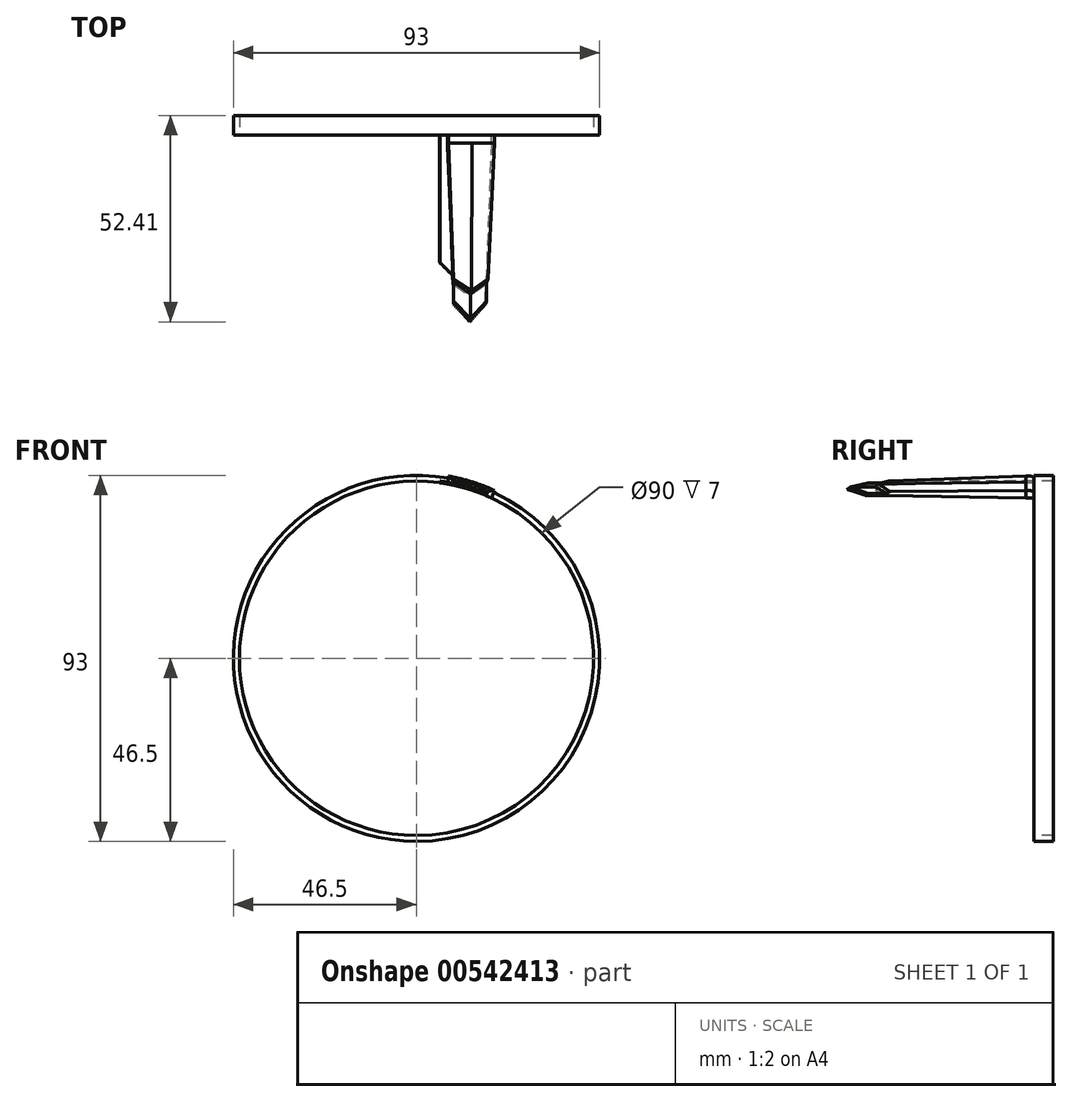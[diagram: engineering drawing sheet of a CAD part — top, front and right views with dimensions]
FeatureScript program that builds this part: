
annotation { "Feature Type Name" : "Feature", "Feature Type Description" : "" }
export const myFeature = defineFeature(function(context is Context, id is Id, definition is map)
    precondition{}
    {
        {
            var Q0;
            Q0=qCreatedBy(makeId("Front.planeOp"),FACE);
            var sketch = newSketch(context, id + "F0", { "sketchPlane" : qUnion([Q0])});
            skCircle(sketch, "E0", {"center": v(0, 0) * mm, "radius": 45 * mm});
            skCircle(sketch, "E1", {"center": v(0, 0) * mm, "radius": 47 * mm});
            skLineSegment(sketch, "E2", {"start": v(0, 0) * mm, "end": v(20, 0) * mm});
            skLineSegment(sketch, "E3", {"start": v(0, 0) * mm, "end": v(8.16, 46.29) * mm});
            skLineSegment(sketch, "E4", {"start": v(0, 0) * mm, "end": v(19.86, 42.6) * mm});
            skCircle(sketch, "E5", {"center": v(0, 0) * mm, "radius": 46.5 * mm});
            skSolve(sketch);
        }
        {
            var Q0;
            {var subQ0=sQuery(id+"F0.wireOp",EDGE,"E3");var subQ1=sQuery(id+"F0.wireOp",EDGE,"E0");var subQ2=makeQuery(id+"F0.imprint","INTERSECT",VERTEX,{"derivedFrom":[subQ1,subQ0]});Q0=makeQuery(id+"F0.imprint","IMPRINT",FACE,{"disambiguationData":[TD([[makeQuery(id+"F0.imprint","IMPRINT",EDGE,{"disambiguationData":[TD([[subQ2,1.0]])],"derivedFrom":subQ1}),-1.0]])]});}
            var Q1;
            {var subQ0=sQuery(id+"F0.wireOp",EDGE,"E3");var subQ1=sQuery(id+"F0.wireOp",EDGE,"E0");var subQ2=makeQuery(id+"F0.imprint","INTERSECT",VERTEX,{"derivedFrom":[subQ1,subQ0]});Q1=makeQuery(id+"F0.imprint","IMPRINT",FACE,{"disambiguationData":[TD([[makeQuery(id+"F0.imprint","IMPRINT",EDGE,{"disambiguationData":[TD([[subQ2,-1.0]])],"derivedFrom":subQ1}),-1.0]])]});}
            extrude(context, id + "F1", {"entities" : qUnion([Q0, Q1]), "oppositeDirection" : true, "depth" : 5 * mm, "offsetDistance" : 25 * mm});
        }
        {
            var Q0;
            {var subQ0=sQuery(id+"F0.wireOp",EDGE,"E3");var subQ1=sQuery(id+"F0.wireOp",EDGE,"E1");var subQ2=makeQuery(id+"F0.imprint","INTERSECT",VERTEX,{"derivedFrom":[subQ1,subQ0]});Q0=makeQuery(id+"F0.imprint","IMPRINT",FACE,{"disambiguationData":[TD([[makeQuery(id+"F0.imprint","IMPRINT",EDGE,{"disambiguationData":[TD([[subQ2,1.0]])],"derivedFrom":subQ1}),1.0]])]});}
            var Q1;
            {var subQ0=sQuery(id+"F0.wireOp",EDGE,"E3");var subQ1=sQuery(id+"F0.wireOp",EDGE,"E0");var subQ2=makeQuery(id+"F0.imprint","INTERSECT",VERTEX,{"derivedFrom":[subQ1,subQ0]});Q1=makeQuery(id+"F0.imprint","IMPRINT",FACE,{"disambiguationData":[TD([[makeQuery(id+"F0.imprint","IMPRINT",EDGE,{"disambiguationData":[TD([[subQ2,1.0]])],"derivedFrom":subQ1}),-1.0]])]});}
            extrude(context, id + "F2", {"entities" : qUnion([Q0, Q1]), "operationType" : NewBodyOperationType.ADD, "depth" : 2 * mm, "offsetDistance" : 25 * mm});
        }
        {
            var Q0;
            {var subQ0=sQuery(id+"F0.wireOp",EDGE,"E3");var subQ1=sQuery(id+"F0.wireOp",EDGE,"E0");var subQ2=makeQuery(id+"F0.imprint","INTERSECT",VERTEX,{"derivedFrom":[subQ1,subQ0]});Q0=makeQuery(id+"F0.imprint","IMPRINT",FACE,{"disambiguationData":[TD([[makeQuery(id+"F0.imprint","IMPRINT",EDGE,{"disambiguationData":[TD([[subQ2,-1.0]])],"derivedFrom":subQ1}),-1.0]])]});}
            cPlane(context, id + "F3", {"entities" : qUnion([Q0]), "cplaneType" : CPlaneType.OFFSET, "offset" : 40 * mm, "width" : 150 * mm, "height" : 150 * mm});
        }
        {
            var Q0;
            Q0=qCreatedBy(id+"F3.planeOp",FACE);
            var sketch = newSketch(context, id + "F4", { "sketchPlane" : qUnion([Q0])});
            skCircle(sketch, "E6", {"center": v(0, 0) * mm, "radius": 45 * mm});
            skArc(sketch, "E7", {"start": v(9.56, 45) * mm, "mid": v(-13.83, -43.87) * mm, "end": v(17.97, 42.34) * mm});
            skLineSegment(sketch, "E8", {"start": v(0, 0) * mm, "end": v(20, 0) * mm});
            skLineSegment(sketch, "E9", {"start": v(0, 0) * mm, "end": v(10.27, 48.3) * mm});
            skLineSegment(sketch, "E10", {"start": v(0, 0) * mm, "end": v(18.87, 44.45) * mm});
            skLineSegment(sketch, "E11", {"start": v(9.56, 45) * mm, "end": v(13.98, 44.35) * mm});
            skLineSegment(sketch, "E12", {"start": v(17.97, 42.34) * mm, "end": v(13.98, 44.35) * mm});
            skSolve(sketch);
        }
        {
            var Q0;
            Q0=makeQuery(id+"F2.opExtrude","CAP_FACE",FACE,{"disambiguationData":[OSD([sQuery(id+"F0.wireOp",EDGE,"E0"),sQuery(id+"F0.wireOp",EDGE,"E1"),sQuery(id+"F0.wireOp",EDGE,"E3"),sQuery(id+"F0.wireOp",EDGE,"E4")])],"isStart":false});
            var sketch = newSketch(context, id + "F5", { "sketchPlane" : qUnion([Q0])});
            skPoint(sketch, "E13", {"position": v(14.13, 44.82) * mm});
            skSolve(sketch);
        }
        {
            var Q1;
            Q1=makeQuery(id+"F5.imprint","IMPRINT",FACE,{"disambiguationData":[TD([[makeQuery(id+"F5.imprint","IMPRINT",EDGE,{"derivedFrom":makeQuery(id+"F2.opExtrude","CAP_EDGE",EDGE,{"disambiguationData":[OSD([sQuery(id+"F0.wireOp",EDGE,"E0")])],"isStart":false})}),-1.0]])]});
            var Q2;
            {var subQ0=sQuery(id+"F4.wireOp",EDGE,"E11");Q2=makeQuery(id+"F4.imprint","IMPRINT",FACE,{"disambiguationData":[TD([[makeQuery(id+"F4.imprint","IMPRINT",EDGE,{"derivedFrom":subQ0}),-1.0]])]});}
            var Q3;
            Q3=sQuery(id+"F5.wireOp",VERTEX,"E13");
            var Q4;
            Q4=sQuery(id+"F4.wireOp",VERTEX,"E12.end");
            loft(context, id + "F6", {"operationType" : NewBodyOperationType.ADD, "sheetProfilesArray" : [{ "sheetProfileEntities" : qUnion([Q1]) }, { "sheetProfileEntities" : qUnion([Q2]) }], "matchConnections" : true, "connections" : [{ "connectionEntities" : qUnion([Q3, Q4]), "connectionEdgeQueries" : qUnion([]), "connectionEdgeParameters" : [] }]});
        }
        {
            var Q0;
            {var subQ0=sQuery(id+"F4.wireOp",EDGE,"E11");Q0=makeQuery(id+"F6.opLoft","CAP_FACE",FACE,{"disambiguationData":[OSD([makeQuery(id+"F4.imprint","IMPRINT",FACE,{"disambiguationData":[TD([[makeQuery(id+"F4.imprint","IMPRINT",EDGE,{"derivedFrom":subQ0}),-1.0]])]})])],"isStart":true});}
            extrude(context, id + "F7", {"entities" : qUnion([Q0]), "operationType" : NewBodyOperationType.ADD, "depth" : 5 * mm, "offsetDistance" : 25 * mm});
        }
        {
            var Q0;
            Q0=makeQuery(id+"F7.opExtrude","CAP_EDGE",EDGE,{"disambiguationData":[OSD([sQuery(id+"F4.wireOp",EDGE,"E6"),sQuery(id+"F4.wireOp",EDGE,"E7"),sQuery(id+"F4.wireOp",EDGE,"E10"),sQuery(id+"F4.wireOp",EDGE,"E12")])],"isStart":false});
            var Q1;
            Q1=makeQuery(id+"F7.opExtrude","CAP_EDGE",EDGE,{"disambiguationData":[OSD([sQuery(id+"F4.wireOp",EDGE,"E6"),sQuery(id+"F4.wireOp",EDGE,"E7"),sQuery(id+"F4.wireOp",EDGE,"E9"),sQuery(id+"F4.wireOp",EDGE,"E11")])],"isStart":false});
            chamfer(context, id + "F8", {"entities" : qUnion([Q0, Q1]), "chamferType" : ChamferType.TWO_OFFSETS, "width1" : 8 * mm, "oppositeDirection" : false, "width2" : 5 * mm, "tangentPropagation" : true});
        }
        {
            var Q0;
            {var subQ0=sQuery(id+"F4.wireOp",EDGE,"E11");var subQ1=sQuery(id+"F4.wireOp",EDGE,"E9");var subQ2=sQuery(id+"F4.wireOp",EDGE,"E7");Q0=makeQuery(id+"F8.opChamfer","BLEND_EDGE",EDGE,{"blendedFrom":[makeQuery(id+"F7.opExtrude","CAP_EDGE",EDGE,{"disambiguationData":[OSD([sQuery(id+"F4.wireOp",EDGE,"E6"),subQ2,subQ1,subQ0])],"isStart":false}),makeQuery(id+"F7.opExtrude","SWEPT_FACE",FACE,{"disambiguationData":[OSD([subQ2,subQ1,subQ0,sQuery(id+"F4.wireOp",EDGE,"E12")])]})],"blendedInto":[makeQuery(id+"F7.opExtrude","SWEPT_FACE",FACE,{"disambiguationData":[OSD([subQ2,subQ1,subQ0,sQuery(id+"F4.wireOp",EDGE,"E12")])]})]});}
            var Q1;
            {var subQ0=sQuery(id+"F4.wireOp",EDGE,"E12");var subQ1=sQuery(id+"F4.wireOp",EDGE,"E10");var subQ2=sQuery(id+"F4.wireOp",EDGE,"E7");Q1=makeQuery(id+"F8.opChamfer","BLEND_EDGE",EDGE,{"blendedFrom":[makeQuery(id+"F7.opExtrude","CAP_EDGE",EDGE,{"disambiguationData":[OSD([sQuery(id+"F4.wireOp",EDGE,"E6"),subQ2,subQ1,subQ0])],"isStart":false}),makeQuery(id+"F7.opExtrude","SWEPT_FACE",FACE,{"disambiguationData":[OSD([subQ2,subQ1,sQuery(id+"F4.wireOp",EDGE,"E11"),subQ0])]})],"blendedInto":[makeQuery(id+"F7.opExtrude","SWEPT_FACE",FACE,{"disambiguationData":[OSD([subQ2,subQ1,sQuery(id+"F4.wireOp",EDGE,"E11"),subQ0])]})]});}
            chamfer(context, id + "F9", {"entities" : qUnion([Q0, Q1]), "width" : 3 * mm});
        }
        {
            var Q0;
            Q0=makeQuery(id+"F2.opExtrude","CAP_EDGE",EDGE,{"disambiguationData":[OSD([sQuery(id+"F0.wireOp",EDGE,"E1")])],"isStart":true});
            fillet(context, id + "F10", {"entities" : qUnion([Q0]), "radius" : 1 * mm, "tangentPropagation" : true, "allowEdgeOverflow" : false});
        }
        {
            var Q0;
            Q0=makeQuery(id+"F2.opExtrude","SWEPT_FACE",FACE,{"disambiguationData":[OSD([sQuery(id+"F0.wireOp",EDGE,"E3")])]});
            var sketch = newSketch(context, id + "F11", { "sketchPlane" : qUnion([Q0])});
            skLineSegment(sketch, "E14.bottom", {"start": v(0, 45) * mm, "end": v(2, 45) * mm});
            skLineSegment(sketch, "E14.top", {"start": v(0, 45.43) * mm, "end": v(2, 45.43) * mm});
            skLineSegment(sketch, "E14.left", {"start": v(0, 45) * mm, "end": v(0, 45.43) * mm});
            skLineSegment(sketch, "E14.right", {"start": v(2, 45) * mm, "end": v(2, 45.43) * mm});
            skLineSegment(sketch, "E15", {"start": v(2, 45.43) * mm, "end": v(35.64, 45.43) * mm});
            skLineSegment(sketch, "E16", {"start": v(35.64, 45.43) * mm, "end": v(35.64, 45) * mm});
            skLineSegment(sketch, "E17", {"start": v(35.64, 45) * mm, "end": v(2, 45) * mm});
            skSolve(sketch);
        }
        {
            var Q0;
            Q0=makeQuery(id+"F11.imprint","IMPRINT",FACE,{"disambiguationData":[TD([[makeQuery(id+"F11.imprint","IMPRINT",EDGE,{"derivedFrom":sQuery(id+"F11.wireOp",EDGE,"E14.right")}),-1.0]])]});
            var Q1;
            Q1=makeQuery(id+"F11.imprint","IMPRINT",FACE,{"disambiguationData":[TD([[makeQuery(id+"F11.imprint","IMPRINT",EDGE,{"derivedFrom":sQuery(id+"F11.wireOp",EDGE,"E14.bottom")}),-1.0]])]});
            var Q2;
            {var subQ0=sQuery(id+"F0.wireOp",EDGE,"E0");Q2=makeQuery(id+"F2.boolean.opBoolean","MERGE",FACE,{"derivedFrom":[makeQuery(id+"F1.opExtrude","SWEPT_FACE",FACE,{"disambiguationData":[OSD([subQ0])]}),makeQuery(id+"F2.opExtrude","SWEPT_FACE",FACE,{"disambiguationData":[OSD([subQ0])]})]});}
            revolve(context, id + "F12", {"operationType" : NewBodyOperationType.ADD, "surfaceOperationType" : NewSurfaceOperationType.NEW, "entities" : qUnion([Q0, Q1]), "axis" : qUnion([Q2]), "revolveType" : RevolveType.SYMMETRIC, "angle" : 5 * degree});
        }
        {
            var Q0;
            Q0=makeQuery(id+"F12.opRevolve","CAP_EDGE",EDGE,{"disambiguationData":[OSD([sQuery(id+"F11.wireOp",EDGE,"E16")])],"isStart":true});
            chamfer(context, id + "F13", {"entities" : qUnion([Q0]), "width" : 3.35 * mm, "tangentPropagation" : true});
        }
        {
            var Q0;
            Q0=qCreatedBy(id+"F3.planeOp",FACE);
            var sketch = newSketch(context, id + "F14", { "sketchPlane" : qUnion([Q0])});
            skCircle(sketch, "E18", {"center": v(0, 0) * mm, "radius": 45.5 * mm});
            skCircle(sketch, "E19", {"center": v(0, 0) * mm, "radius": 45 * mm});
            skLineSegment(sketch, "E20", {"start": v(0, 0) * mm, "end": v(20, 0) * mm});
            skLineSegment(sketch, "E21", {"start": v(0, 0) * mm, "end": v(9.46, 44.5) * mm});
            skLineSegment(sketch, "E22", {"start": v(0, 0) * mm, "end": v(17.78, 41.88) * mm});
            skLineSegment(sketch, "E23", {"start": v(0, 0) * mm, "end": v(13.73, 43.56) * mm});
            skLineSegment(sketch, "E24", {"start": v(9.46, 44.5) * mm, "end": v(13.73, 43.56) * mm});
            skLineSegment(sketch, "E25", {"start": v(13.73, 43.56) * mm, "end": v(17.78, 41.88) * mm});
            skSolve(sketch);
        }
        {
            var Q0;
            {var subQ0=sQuery(id+"F14.wireOp",EDGE,"E25");var subQ1=sQuery(id+"F14.wireOp",EDGE,"E18");var subQ2=makeQuery(id+"F14.imprint","INTERSECT",VERTEX,{"derivedFrom":[subQ1,subQ0]});Q0=makeQuery(id+"F14.imprint","IMPRINT",FACE,{"disambiguationData":[TD([[makeQuery(id+"F14.imprint","IMPRINT",EDGE,{"disambiguationData":[TD([[subQ2,-1.0]])],"derivedFrom":subQ1}),-1.0]])]});}
            var Q1;
            {var subQ0=sQuery(id+"F14.wireOp",EDGE,"E24");var subQ1=sQuery(id+"F14.wireOp",EDGE,"E18");var subQ2=makeQuery(id+"F14.imprint","INTERSECT",VERTEX,{"derivedFrom":[subQ1,subQ0]});Q1=makeQuery(id+"F14.imprint","IMPRINT",FACE,{"disambiguationData":[TD([[makeQuery(id+"F14.imprint","IMPRINT",EDGE,{"disambiguationData":[TD([[subQ2,1.0]])],"derivedFrom":subQ1}),-1.0]])]});}
            var Q2;
            {var subQ1=sQuery(id+"F14.wireOp",EDGE,"E18");var subQ5=sQuery(id+"F14.wireOp",EDGE,"E24");var subQ6=makeQuery(id+"F14.imprint","INTERSECT",VERTEX,{"derivedFrom":[subQ1,subQ5]});Q2=makeQuery(id+"F14.imprint","IMPRINT",FACE,{"disambiguationData":[TD([[makeQuery(id+"F14.imprint","IMPRINT",EDGE,{"disambiguationData":[TD([[subQ6,1.0]])],"derivedFrom":subQ1}),1.0]])]});}
            var Q3;
            {var subQ1=sQuery(id+"F14.wireOp",EDGE,"E18");var subQ7=sQuery(id+"F14.wireOp",EDGE,"E25");var subQ9=makeQuery(id+"F14.imprint","INTERSECT",VERTEX,{"derivedFrom":[subQ1,subQ7]});Q3=makeQuery(id+"F14.imprint","IMPRINT",FACE,{"disambiguationData":[TD([[makeQuery(id+"F14.imprint","IMPRINT",EDGE,{"disambiguationData":[TD([[subQ9,-1.0]])],"derivedFrom":subQ1}),1.0]])]});}
            extrude(context, id + "F15", {"entities" : qUnion([Q0, Q1, Q2, Q3]), "operationType" : NewBodyOperationType.ADD, "endBound" : BoundingType.SYMMETRIC, "depth" : 20 * mm, "offsetDistance" : 25 * mm});
        }
        {
            var Q0;
            Q0=makeQuery(id+"F15.opExtrude","CAP_EDGE",EDGE,{"disambiguationData":[OSD([sQuery(id+"F14.wireOp",EDGE,"E21")])],"isStart":false});
            var Q1;
            Q1=makeQuery(id+"F15.opExtrude","CAP_EDGE",EDGE,{"disambiguationData":[OSD([sQuery(id+"F14.wireOp",EDGE,"E22")])],"isStart":false});
            chamfer(context, id + "F16", {"entities" : qUnion([Q0, Q1]), "width" : 5 * mm, "tangentPropagation" : true});
        }
        {
            var Q0;
            Q0=makeQuery(id+"F16.opChamfer","BLEND_EDGE",EDGE,{"blendedFrom":[makeQuery(id+"F15.opExtrude","CAP_EDGE",EDGE,{"disambiguationData":[OSD([sQuery(id+"F14.wireOp",EDGE,"E21")])],"isStart":false}),makeQuery(id+"F15.opExtrude","SWEPT_FACE",FACE,{"disambiguationData":[OSD([sQuery(id+"F14.wireOp",EDGE,"E24")])]})],"blendedInto":[makeQuery(id+"F15.opExtrude","SWEPT_FACE",FACE,{"disambiguationData":[OSD([sQuery(id+"F14.wireOp",EDGE,"E24")])]})]});
            var Q1;
            Q1=makeQuery(id+"F16.opChamfer","BLEND_EDGE",EDGE,{"blendedFrom":[makeQuery(id+"F15.opExtrude","CAP_EDGE",EDGE,{"disambiguationData":[OSD([sQuery(id+"F14.wireOp",EDGE,"E22")])],"isStart":false}),makeQuery(id+"F15.opExtrude","SWEPT_FACE",FACE,{"disambiguationData":[OSD([sQuery(id+"F14.wireOp",EDGE,"E25")])]})],"blendedInto":[makeQuery(id+"F15.opExtrude","SWEPT_FACE",FACE,{"disambiguationData":[OSD([sQuery(id+"F14.wireOp",EDGE,"E25")])]})]});
            chamfer(context, id + "F17", {"entities" : qUnion([Q0, Q1]), "width" : 2 * mm, "tangentPropagation" : true});
        }
    });
